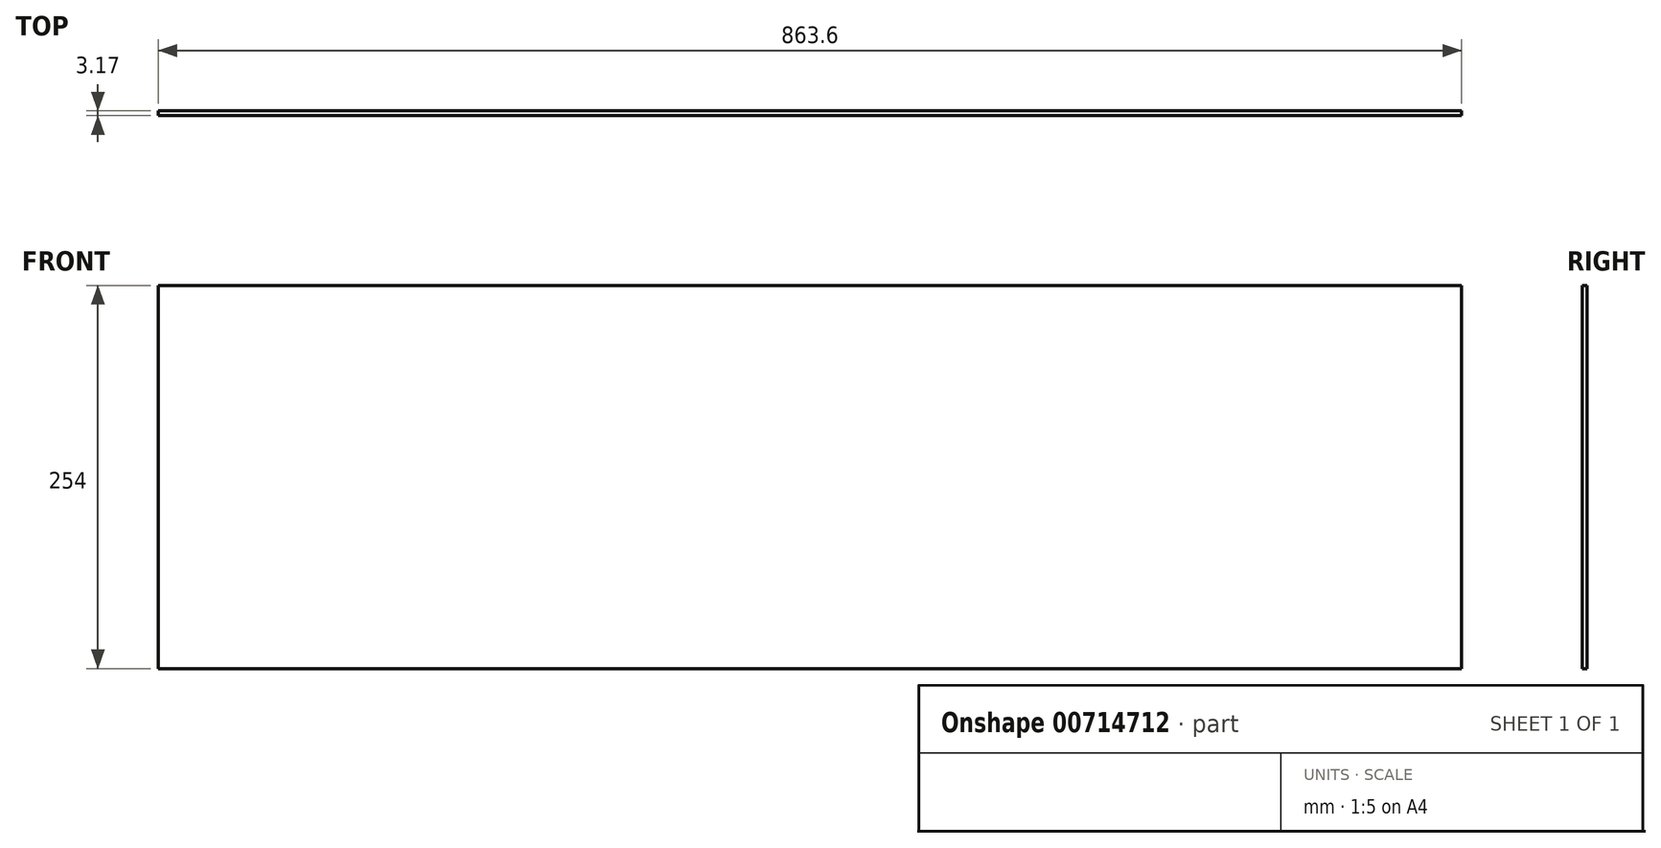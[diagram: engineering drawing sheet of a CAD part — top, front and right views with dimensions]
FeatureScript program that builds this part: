
annotation { "Feature Type Name" : "Feature", "Feature Type Description" : "" }
export const myFeature = defineFeature(function(context is Context, id is Id, definition is map)
    precondition{}
    {
        {
            var Q0;
            Q0=qCreatedBy(makeId("Front.planeOp"),FACE);
            var sketch = newSketch(context, id + "F0", { "sketchPlane" : qUnion([Q0])});
            skLineSegment(sketch, "E0.bottom", {"start": v(431.8, 127) * mm, "end": v(-431.8, 127) * mm});
            skLineSegment(sketch, "E0.top", {"start": v(431.8, -127) * mm, "end": v(-431.8, -127) * mm});
            skLineSegment(sketch, "E0.left", {"start": v(431.8, 127) * mm, "end": v(431.8, -127) * mm});
            skLineSegment(sketch, "E0.right", {"start": v(-431.8, 127) * mm, "end": v(-431.8, -127) * mm});
            skPoint(sketch, "E0.middle", {"position": v(0, 0) * mm});
            skSolve(sketch);
        }
        {
            var Q0;
            Q0 = qSketchRegion(id + "F0", true);
            extrude(context, id + "F1", {"entities" : qUnion([Q0]), "depth" : 3.17 * mm, "offsetDistance" : 25.4 * mm});
        }
    });
